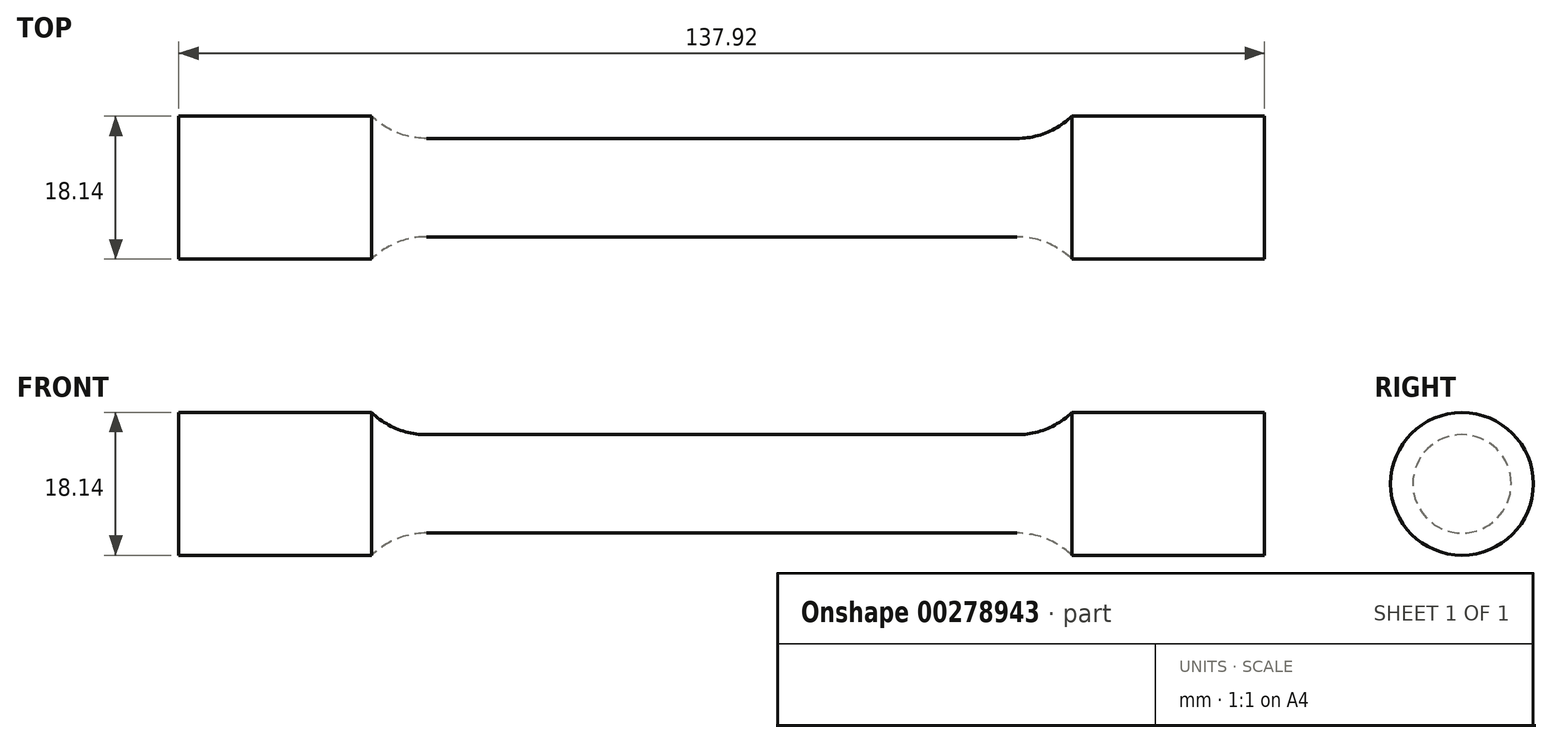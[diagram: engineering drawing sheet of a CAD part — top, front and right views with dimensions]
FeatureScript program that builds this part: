
annotation { "Feature Type Name" : "Feature", "Feature Type Description" : "" }
export const myFeature = defineFeature(function(context is Context, id is Id, definition is map)
    precondition{}
    {
        {
            var Q0;
            Q0=qCreatedBy(makeId("Front.planeOp"),FACE);
            var sketch = newSketch(context, id + "F0", { "sketchPlane" : qUnion([Q0])});
            skLineSegment(sketch, "E0", {"start": v(0, 6.25) * mm, "end": v(37.5, 6.25) * mm});
            skArc(sketch, "E1", {"start": v(37.5, 6.25) * mm, "mid": v(41.25, 6.98) * mm, "end": v(44.46, 9.07) * mm});
            skLineSegment(sketch, "E2", {"start": v(44.46, 9.07) * mm, "end": v(68.96, 9.07) * mm});
            skLineSegment(sketch, "E3", {"start": v(68.96, 9.07) * mm, "end": v(68.96, 0) * mm});
            skLineSegment(sketch, "E4.MirrorCS", {"start": v(0, 6.25) * mm, "end": v(-37.5, 6.25) * mm});
            skLineSegment(sketch, "E5.MirrorCS", {"start": v(-68.96, 9.07) * mm, "end": v(-68.96, 0) * mm});
            skLineSegment(sketch, "E6.MirrorCS", {"start": v(-44.46, 9.07) * mm, "end": v(-68.96, 9.07) * mm});
            skArc(sketch, "E7.MirrorCS", {"start": v(-37.5, 6.25) * mm, "mid": v(-41.25, 6.98) * mm, "end": v(-44.46, 9.07) * mm});
            skLineSegment(sketch, "E8", {"start": v(-68.96, 0) * mm, "end": v(68.96, 0) * mm});
            skSolve(sketch);
        }
        {
            var Q0;
            Q0 = qSketchRegion(id + "F0", true);
            var Q1;
            Q1=sQuery(id+"F0.wireOp",EDGE,"E8");
            revolve(context, id + "F1", {"entities" : qUnion([Q0]), "axis" : qUnion([Q1]), "revolveType" : RevolveType.FULL});
        }
    });
